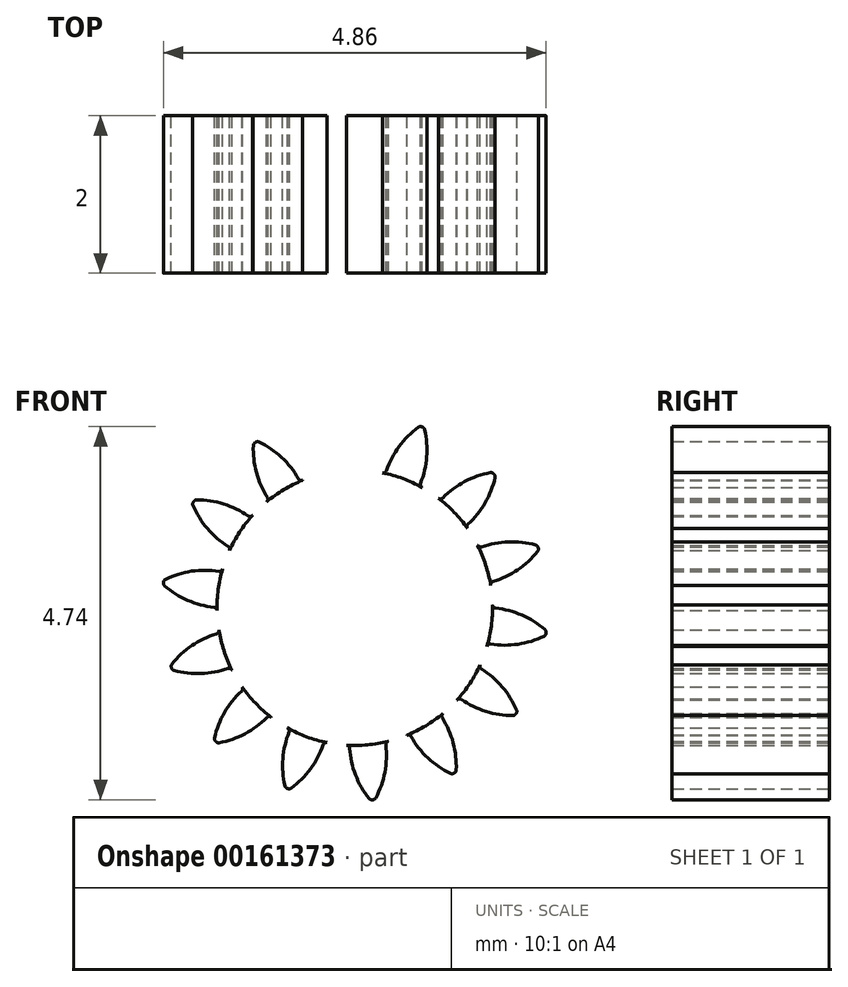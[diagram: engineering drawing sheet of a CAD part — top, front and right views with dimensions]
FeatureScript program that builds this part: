
annotation { "Feature Type Name" : "Feature", "Feature Type Description" : "" }
export const myFeature = defineFeature(function(context is Context, id is Id, definition is map)
    precondition{}
    {
        {
            var Q0;
            Q0=qCreatedBy(makeId("Front.planeOp"),FACE);
            var sketch = newSketch(context, id + "F0", { "sketchPlane" : qUnion([Q0])});
            skCircle(sketch, "E0", {"center": v(0, 0) * mm, "radius": 1.75 * mm, "construction": true});
            skCircle(sketch, "E1", {"center": v(0, 0) * mm, "radius": 2.1 * mm, "construction": true});
            skCircle(sketch, "E2", {"center": v(0, 0) * mm, "radius": 2.45 * mm, "construction": true});
            skLineSegment(sketch, "E3", {"start": v(0, 0) * mm, "end": v(0, 10.28) * mm, "construction": true});
            skLineSegment(sketch, "E4", {"start": v(0, 0) * mm, "end": v(-1.03, 11.12) * mm, "construction": true});
            skLineSegment(sketch, "E5", {"start": v(0, 2.1) * mm, "end": v(-15.76, 2.1) * mm, "construction": true});
            skLineSegment(sketch, "E6", {"start": v(0, 2.1) * mm, "end": v(-14.39, -3.14) * mm, "construction": true});
            skCircle(sketch, "E7", {"center": v(0, 2.1) * mm, "radius": 1.15 * mm, "construction": true});
            skCircle(sketch, "E8", {"center": v(-1.08, 1.7) * mm, "radius": 1.15 * mm, "construction": true});
            skArc(sketch, "E9", {"start": v(-0.18, 2.42) * mm, "mid": v(0, 2.12) * mm, "end": v(0.07, 1.79) * mm});
            skArc(sketch, "E10.MirrorCS", {"start": v(-0.27, 2.42) * mm, "mid": v(-0.38, 2.09) * mm, "end": v(-0.4, 1.74) * mm});
            skArc(sketch, "E11", {"start": v(-0.23, 2.44) * mm, "mid": v(-0.23, 2.44) * mm, "end": v(-0.22, 2.44) * mm});
            skArc(sketch, "E12", {"start": v(-0.43, 1.7) * mm, "mid": v(0.16, -1.74) * mm, "end": v(0.1, 1.75) * mm});
            skPoint(sketch, "E13.visualSharp", {"position": v(-0.39, 1.7) * mm});
            skArc(sketch, "E13.filletArc", {"start": v(-0.43, 1.7) * mm, "mid": v(-0.4, 1.71) * mm, "end": v(-0.4, 1.74) * mm});
            skPoint(sketch, "E14.visualSharp", {"position": v(-0.26, 2.44) * mm});
            skArc(sketch, "E14.filletArc", {"start": v(-0.23, 2.44) * mm, "mid": v(-0.25, 2.43) * mm, "end": v(-0.27, 2.42) * mm});
            skPoint(sketch, "E15.visualSharp", {"position": v(-0.2, 2.44) * mm});
            skArc(sketch, "E15.filletArc", {"start": v(-0.18, 2.42) * mm, "mid": v(-0.2, 2.44) * mm, "end": v(-0.22, 2.44) * mm});
            skPoint(sketch, "E16.visualSharp", {"position": v(0.07, 1.75) * mm});
            skArc(sketch, "E16.filletArc", {"start": v(0.07, 1.79) * mm, "mid": v(0.08, 1.76) * mm, "end": v(0.1, 1.75) * mm});
            skArc(sketch, "E17.1.0", {"start": v(-1.12, 1.34) * mm, "mid": v(-1.1, 1.37) * mm, "end": v(-1.11, 1.4) * mm});
            skArc(sketch, "E17.1.1", {"start": v(-1.29, 2.06) * mm, "mid": v(-1.25, 1.72) * mm, "end": v(-1.11, 1.4) * mm});
            skArc(sketch, "E17.1.2", {"start": v(-1.27, 2.1) * mm, "mid": v(-1.28, 2.08) * mm, "end": v(-1.29, 2.06) * mm});
            skArc(sketch, "E17.1.3", {"start": v(-1.27, 2.1) * mm, "mid": v(-1.26, 2.1) * mm, "end": v(-1.26, 2.1) * mm});
            skArc(sketch, "E17.1.4", {"start": v(-1.22, 2.1) * mm, "mid": v(-1.24, 2.1) * mm, "end": v(-1.26, 2.1) * mm});
            skArc(sketch, "E17.1.5", {"start": v(-1.22, 2.1) * mm, "mid": v(-0.93, 1.9) * mm, "end": v(-0.71, 1.64) * mm});
            skArc(sketch, "E17.1.6", {"start": v(-0.71, 1.64) * mm, "mid": v(-0.7, 1.62) * mm, "end": v(-0.66, 1.62) * mm});
            skArc(sketch, "E17.2.0", {"start": v(-1.6, 0.73) * mm, "mid": v(-1.6, 0.76) * mm, "end": v(-1.6, 0.78) * mm});
            skArc(sketch, "E17.2.1", {"start": v(-2.06, 1.3) * mm, "mid": v(-1.87, 1) * mm, "end": v(-1.6, 0.78) * mm});
            skArc(sketch, "E17.2.2", {"start": v(-2.05, 1.34) * mm, "mid": v(-2.06, 1.32) * mm, "end": v(-2.06, 1.3) * mm});
            skArc(sketch, "E17.2.3", {"start": v(-2.05, 1.34) * mm, "mid": v(-2.05, 1.34) * mm, "end": v(-2.04, 1.35) * mm});
            skArc(sketch, "E17.2.4", {"start": v(-2, 1.37) * mm, "mid": v(-2.03, 1.36) * mm, "end": v(-2.04, 1.35) * mm});
            skArc(sketch, "E17.2.5", {"start": v(-2, 1.37) * mm, "mid": v(-1.67, 1.32) * mm, "end": v(-1.35, 1.17) * mm});
            skArc(sketch, "E17.2.6", {"start": v(-1.35, 1.17) * mm, "mid": v(-1.33, 1.16) * mm, "end": v(-1.3, 1.17) * mm});
            skArc(sketch, "E17.3.0", {"start": v(-1.75, -0.04) * mm, "mid": v(-1.76, 0) * mm, "end": v(-1.79, 0) * mm});
            skArc(sketch, "E17.3.1", {"start": v(-2.42, 0.28) * mm, "mid": v(-2.12, 0.1) * mm, "end": v(-1.79, 0) * mm});
            skArc(sketch, "E17.3.2", {"start": v(-2.43, 0.32) * mm, "mid": v(-2.43, 0.3) * mm, "end": v(-2.42, 0.28) * mm});
            skArc(sketch, "E17.3.3", {"start": v(-2.43, 0.32) * mm, "mid": v(-2.43, 0.32) * mm, "end": v(-2.43, 0.33) * mm});
            skArc(sketch, "E17.3.4", {"start": v(-2.4, 0.36) * mm, "mid": v(-2.42, 0.35) * mm, "end": v(-2.43, 0.33) * mm});
            skArc(sketch, "E17.3.5", {"start": v(-2.4, 0.36) * mm, "mid": v(-2.07, 0.46) * mm, "end": v(-1.73, 0.46) * mm});
            skArc(sketch, "E17.3.6", {"start": v(-1.73, 0.46) * mm, "mid": v(-1.7, 0.47) * mm, "end": v(-1.68, 0.5) * mm});
            skArc(sketch, "E17.4.0", {"start": v(-1.56, -0.8) * mm, "mid": v(-1.58, -0.77) * mm, "end": v(-1.61, -0.77) * mm});
            skArc(sketch, "E17.4.1", {"start": v(-2.3, -0.8) * mm, "mid": v(-1.95, -0.84) * mm, "end": v(-1.61, -0.77) * mm});
            skArc(sketch, "E17.4.2", {"start": v(-2.33, -0.77) * mm, "mid": v(-2.31, -0.79) * mm, "end": v(-2.3, -0.8) * mm});
            skArc(sketch, "E17.4.3", {"start": v(-2.33, -0.77) * mm, "mid": v(-2.33, -0.76) * mm, "end": v(-2.33, -0.76) * mm});
            skArc(sketch, "E17.4.4", {"start": v(-2.32, -0.72) * mm, "mid": v(-2.33, -0.74) * mm, "end": v(-2.33, -0.76) * mm});
            skArc(sketch, "E17.4.5", {"start": v(-2.32, -0.72) * mm, "mid": v(-2.07, -0.48) * mm, "end": v(-1.76, -0.33) * mm});
            skArc(sketch, "E17.4.6", {"start": v(-1.76, -0.33) * mm, "mid": v(-1.73, -0.31) * mm, "end": v(-1.73, -0.29) * mm});
            skArc(sketch, "E17.5.0", {"start": v(-1.06, -1.4) * mm, "mid": v(-1.1, -1.38) * mm, "end": v(-1.12, -1.4) * mm});
            skArc(sketch, "E17.5.1", {"start": v(-1.72, -1.72) * mm, "mid": v(-1.4, -1.6) * mm, "end": v(-1.12, -1.4) * mm});
            skArc(sketch, "E17.5.2", {"start": v(-1.76, -1.7) * mm, "mid": v(-1.74, -1.71) * mm, "end": v(-1.72, -1.72) * mm});
            skArc(sketch, "E17.5.3", {"start": v(-1.76, -1.7) * mm, "mid": v(-1.77, -1.7) * mm, "end": v(-1.77, -1.7) * mm});
            skArc(sketch, "E17.5.4", {"start": v(-1.78, -1.65) * mm, "mid": v(-1.78, -1.67) * mm, "end": v(-1.77, -1.7) * mm});
            skArc(sketch, "E17.5.5", {"start": v(-1.78, -1.65) * mm, "mid": v(-1.66, -1.33) * mm, "end": v(-1.44, -1.06) * mm});
            skArc(sketch, "E17.5.6", {"start": v(-1.44, -1.06) * mm, "mid": v(-1.42, -1.03) * mm, "end": v(-1.43, -1) * mm});
            skArc(sketch, "E17.6.0", {"start": v(-0.35, -1.71) * mm, "mid": v(-0.38, -1.72) * mm, "end": v(-0.4, -1.74) * mm});
            skArc(sketch, "E17.6.1", {"start": v(-0.8, -2.3) * mm, "mid": v(-0.56, -2.05) * mm, "end": v(-0.4, -1.74) * mm});
            skArc(sketch, "E17.6.2", {"start": v(-0.85, -2.3) * mm, "mid": v(-0.83, -2.3) * mm, "end": v(-0.8, -2.3) * mm});
            skArc(sketch, "E17.6.3", {"start": v(-0.85, -2.3) * mm, "mid": v(-0.85, -2.3) * mm, "end": v(-0.86, -2.3) * mm});
            skArc(sketch, "E17.6.4", {"start": v(-0.89, -2.26) * mm, "mid": v(-0.88, -2.28) * mm, "end": v(-0.86, -2.3) * mm});
            skArc(sketch, "E17.6.5", {"start": v(-0.89, -2.26) * mm, "mid": v(-0.91, -1.92) * mm, "end": v(-0.83, -1.58) * mm});
            skArc(sketch, "E17.6.6", {"start": v(-0.83, -1.58) * mm, "mid": v(-0.83, -1.55) * mm, "end": v(-0.85, -1.53) * mm});
            skArc(sketch, "E17.7.0", {"start": v(0.43, -1.7) * mm, "mid": v(0.4, -1.71) * mm, "end": v(0.4, -1.74) * mm});
            skArc(sketch, "E17.7.1", {"start": v(0.27, -2.42) * mm, "mid": v(0.38, -2.09) * mm, "end": v(0.4, -1.74) * mm});
            skArc(sketch, "E17.7.2", {"start": v(0.23, -2.44) * mm, "mid": v(0.25, -2.43) * mm, "end": v(0.27, -2.42) * mm});
            skArc(sketch, "E17.7.3", {"start": v(0.23, -2.44) * mm, "mid": v(0.23, -2.44) * mm, "end": v(0.22, -2.44) * mm});
            skArc(sketch, "E17.7.4", {"start": v(0.18, -2.42) * mm, "mid": v(0.2, -2.44) * mm, "end": v(0.22, -2.44) * mm});
            skArc(sketch, "E17.7.5", {"start": v(0.18, -2.42) * mm, "mid": v(0, -2.12) * mm, "end": v(-0.07, -1.79) * mm});
            skArc(sketch, "E17.7.6", {"start": v(-0.07, -1.79) * mm, "mid": v(-0.08, -1.76) * mm, "end": v(-0.1, -1.75) * mm});
            skArc(sketch, "E17.8.0", {"start": v(1.12, -1.34) * mm, "mid": v(1.1, -1.37) * mm, "end": v(1.11, -1.4) * mm});
            skArc(sketch, "E17.8.1", {"start": v(1.29, -2.06) * mm, "mid": v(1.25, -1.72) * mm, "end": v(1.11, -1.4) * mm});
            skArc(sketch, "E17.8.2", {"start": v(1.27, -2.1) * mm, "mid": v(1.28, -2.08) * mm, "end": v(1.29, -2.06) * mm});
            skArc(sketch, "E17.8.3", {"start": v(1.27, -2.1) * mm, "mid": v(1.26, -2.1) * mm, "end": v(1.26, -2.1) * mm});
            skArc(sketch, "E17.8.4", {"start": v(1.22, -2.1) * mm, "mid": v(1.24, -2.1) * mm, "end": v(1.26, -2.1) * mm});
            skArc(sketch, "E17.8.5", {"start": v(1.22, -2.1) * mm, "mid": v(0.93, -1.9) * mm, "end": v(0.71, -1.64) * mm});
            skArc(sketch, "E17.8.6", {"start": v(0.71, -1.64) * mm, "mid": v(0.7, -1.62) * mm, "end": v(0.66, -1.62) * mm});
            skArc(sketch, "E17.9.0", {"start": v(1.6, -0.73) * mm, "mid": v(1.6, -0.76) * mm, "end": v(1.6, -0.78) * mm});
            skArc(sketch, "E17.9.1", {"start": v(2.06, -1.3) * mm, "mid": v(1.87, -1) * mm, "end": v(1.6, -0.78) * mm});
            skArc(sketch, "E17.9.2", {"start": v(2.05, -1.34) * mm, "mid": v(2.06, -1.32) * mm, "end": v(2.06, -1.3) * mm});
            skArc(sketch, "E17.9.3", {"start": v(2.05, -1.34) * mm, "mid": v(2.05, -1.34) * mm, "end": v(2.04, -1.35) * mm});
            skArc(sketch, "E17.9.4", {"start": v(2, -1.37) * mm, "mid": v(2.03, -1.36) * mm, "end": v(2.04, -1.35) * mm});
            skArc(sketch, "E17.9.5", {"start": v(2, -1.37) * mm, "mid": v(1.67, -1.32) * mm, "end": v(1.35, -1.17) * mm});
            skArc(sketch, "E17.9.6", {"start": v(1.35, -1.17) * mm, "mid": v(1.33, -1.16) * mm, "end": v(1.3, -1.17) * mm});
            skArc(sketch, "E17.10.0", {"start": v(1.75, 0.04) * mm, "mid": v(1.76, 0) * mm, "end": v(1.79, 0) * mm});
            skArc(sketch, "E17.10.1", {"start": v(2.42, -0.28) * mm, "mid": v(2.12, -0.1) * mm, "end": v(1.79, 0) * mm});
            skArc(sketch, "E17.10.2", {"start": v(2.43, -0.32) * mm, "mid": v(2.43, -0.3) * mm, "end": v(2.42, -0.28) * mm});
            skArc(sketch, "E17.10.3", {"start": v(2.43, -0.32) * mm, "mid": v(2.43, -0.32) * mm, "end": v(2.43, -0.33) * mm});
            skArc(sketch, "E17.10.4", {"start": v(2.4, -0.36) * mm, "mid": v(2.42, -0.35) * mm, "end": v(2.43, -0.33) * mm});
            skArc(sketch, "E17.10.5", {"start": v(2.4, -0.36) * mm, "mid": v(2.07, -0.46) * mm, "end": v(1.73, -0.46) * mm});
            skArc(sketch, "E17.10.6", {"start": v(1.73, -0.46) * mm, "mid": v(1.7, -0.47) * mm, "end": v(1.68, -0.5) * mm});
            skArc(sketch, "E17.11.0", {"start": v(1.56, 0.8) * mm, "mid": v(1.58, 0.77) * mm, "end": v(1.61, 0.77) * mm});
            skArc(sketch, "E17.11.1", {"start": v(2.3, 0.8) * mm, "mid": v(1.95, 0.84) * mm, "end": v(1.61, 0.77) * mm});
            skArc(sketch, "E17.11.2", {"start": v(2.33, 0.77) * mm, "mid": v(2.31, 0.79) * mm, "end": v(2.3, 0.8) * mm});
            skArc(sketch, "E17.11.3", {"start": v(2.33, 0.77) * mm, "mid": v(2.33, 0.76) * mm, "end": v(2.33, 0.76) * mm});
            skArc(sketch, "E17.11.4", {"start": v(2.32, 0.72) * mm, "mid": v(2.33, 0.74) * mm, "end": v(2.33, 0.76) * mm});
            skArc(sketch, "E17.11.5", {"start": v(2.32, 0.72) * mm, "mid": v(2.07, 0.48) * mm, "end": v(1.76, 0.33) * mm});
            skArc(sketch, "E17.11.6", {"start": v(1.76, 0.33) * mm, "mid": v(1.73, 0.31) * mm, "end": v(1.73, 0.29) * mm});
            skArc(sketch, "E17.12.0", {"start": v(1.06, 1.4) * mm, "mid": v(1.1, 1.38) * mm, "end": v(1.12, 1.4) * mm});
            skArc(sketch, "E17.12.1", {"start": v(1.72, 1.72) * mm, "mid": v(1.4, 1.6) * mm, "end": v(1.12, 1.4) * mm});
            skArc(sketch, "E17.12.2", {"start": v(1.76, 1.7) * mm, "mid": v(1.74, 1.71) * mm, "end": v(1.72, 1.72) * mm});
            skArc(sketch, "E17.12.3", {"start": v(1.76, 1.7) * mm, "mid": v(1.77, 1.7) * mm, "end": v(1.77, 1.7) * mm});
            skArc(sketch, "E17.12.4", {"start": v(1.78, 1.65) * mm, "mid": v(1.78, 1.67) * mm, "end": v(1.77, 1.7) * mm});
            skArc(sketch, "E17.12.5", {"start": v(1.78, 1.65) * mm, "mid": v(1.66, 1.33) * mm, "end": v(1.44, 1.06) * mm});
            skArc(sketch, "E17.12.6", {"start": v(1.44, 1.06) * mm, "mid": v(1.42, 1.03) * mm, "end": v(1.43, 1) * mm});
            skArc(sketch, "E17.13.0", {"start": v(0.35, 1.71) * mm, "mid": v(0.38, 1.72) * mm, "end": v(0.4, 1.74) * mm});
            skArc(sketch, "E17.13.1", {"start": v(0.8, 2.3) * mm, "mid": v(0.56, 2.05) * mm, "end": v(0.4, 1.74) * mm});
            skArc(sketch, "E17.13.2", {"start": v(0.85, 2.3) * mm, "mid": v(0.83, 2.3) * mm, "end": v(0.8, 2.3) * mm});
            skArc(sketch, "E17.13.3", {"start": v(0.85, 2.3) * mm, "mid": v(0.85, 2.3) * mm, "end": v(0.86, 2.3) * mm});
            skArc(sketch, "E17.13.4", {"start": v(0.89, 2.26) * mm, "mid": v(0.88, 2.28) * mm, "end": v(0.86, 2.3) * mm});
            skArc(sketch, "E17.13.5", {"start": v(0.89, 2.26) * mm, "mid": v(0.91, 1.92) * mm, "end": v(0.83, 1.58) * mm});
            skArc(sketch, "E17.13.6", {"start": v(0.83, 1.58) * mm, "mid": v(0.83, 1.55) * mm, "end": v(0.85, 1.53) * mm});
            skSolve(sketch);
        }
        {
            var Q0;
            Q0=makeQuery(id+"F0.imprint","IMPRINT",FACE,{"disambiguationData":[TD([[makeQuery(id+"F0.imprint","IMPRINT",EDGE,{"derivedFrom":sQuery(id+"F0.wireOp",EDGE,"E9")}),-1.0]])]});
            var Q1;
            {var subQ0=sQuery(id+"F0.wireOp",EDGE,"E17.1.0");Q1=makeQuery(id+"F0.imprint","IMPRINT",FACE,{"disambiguationData":[TD([[makeQuery(id+"F0.imprint","IMPRINT",EDGE,{"derivedFrom":subQ0}),-1.0]])]});}
            var Q2;
            {var subQ0=sQuery(id+"F0.wireOp",EDGE,"E17.2.0");Q2=makeQuery(id+"F0.imprint","IMPRINT",FACE,{"disambiguationData":[TD([[makeQuery(id+"F0.imprint","IMPRINT",EDGE,{"derivedFrom":subQ0}),-1.0]])]});}
            var Q3;
            {var subQ0=sQuery(id+"F0.wireOp",EDGE,"E17.3.0");Q3=makeQuery(id+"F0.imprint","IMPRINT",FACE,{"disambiguationData":[TD([[makeQuery(id+"F0.imprint","IMPRINT",EDGE,{"derivedFrom":subQ0}),-1.0]])]});}
            var Q4;
            {var subQ0=sQuery(id+"F0.wireOp",EDGE,"E17.4.0");Q4=makeQuery(id+"F0.imprint","IMPRINT",FACE,{"disambiguationData":[TD([[makeQuery(id+"F0.imprint","IMPRINT",EDGE,{"derivedFrom":subQ0}),-1.0]])]});}
            var Q5;
            {var subQ0=sQuery(id+"F0.wireOp",EDGE,"E17.16.0");Q5=makeQuery(id+"F0.imprint","IMPRINT",FACE,{"disambiguationData":[TD([[makeQuery(id+"F0.imprint","IMPRINT",EDGE,{"derivedFrom":subQ0}),-1.0]])]});}
            var Q6;
            {var subQ0=sQuery(id+"F0.wireOp",EDGE,"E17.15.0");Q6=makeQuery(id+"F0.imprint","IMPRINT",FACE,{"disambiguationData":[TD([[makeQuery(id+"F0.imprint","IMPRINT",EDGE,{"derivedFrom":subQ0}),-1.0]])]});}
            var Q7;
            {var subQ1=sQuery(id+"F0.wireOp",EDGE,"E17.14.0");Q7=makeQuery(id+"F0.imprint","IMPRINT",FACE,{"disambiguationData":[TD([[makeQuery(id+"F0.imprint","IMPRINT",EDGE,{"derivedFrom":subQ1}),-1.0]])]});}
            var Q8;
            {var subQ0=sQuery(id+"F0.wireOp",EDGE,"E17.13.0");Q8=makeQuery(id+"F0.imprint","IMPRINT",FACE,{"disambiguationData":[TD([[makeQuery(id+"F0.imprint","IMPRINT",EDGE,{"derivedFrom":subQ0}),-1.0]])]});}
            var Q9;
            {var subQ1=sQuery(id+"F0.wireOp",EDGE,"E17.12.0");Q9=makeQuery(id+"F0.imprint","IMPRINT",FACE,{"disambiguationData":[TD([[makeQuery(id+"F0.imprint","IMPRINT",EDGE,{"derivedFrom":subQ1}),-1.0]])]});}
            var Q10;
            {var subQ0=sQuery(id+"F0.wireOp",EDGE,"E17.11.0");Q10=makeQuery(id+"F0.imprint","IMPRINT",FACE,{"disambiguationData":[TD([[makeQuery(id+"F0.imprint","IMPRINT",EDGE,{"derivedFrom":subQ0}),-1.0]])]});}
            var Q11;
            {var subQ0=sQuery(id+"F0.wireOp",EDGE,"E17.10.0");Q11=makeQuery(id+"F0.imprint","IMPRINT",FACE,{"disambiguationData":[TD([[makeQuery(id+"F0.imprint","IMPRINT",EDGE,{"derivedFrom":subQ0}),-1.0]])]});}
            var Q12;
            {var subQ0=sQuery(id+"F0.wireOp",EDGE,"E17.9.0");Q12=makeQuery(id+"F0.imprint","IMPRINT",FACE,{"disambiguationData":[TD([[makeQuery(id+"F0.imprint","IMPRINT",EDGE,{"derivedFrom":subQ0}),-1.0]])]});}
            var Q13;
            {var subQ0=sQuery(id+"F0.wireOp",EDGE,"E17.8.0");Q13=makeQuery(id+"F0.imprint","IMPRINT",FACE,{"disambiguationData":[TD([[makeQuery(id+"F0.imprint","IMPRINT",EDGE,{"derivedFrom":subQ0}),-1.0]])]});}
            var Q14;
            {var subQ0=sQuery(id+"F0.wireOp",EDGE,"E17.7.0");Q14=makeQuery(id+"F0.imprint","IMPRINT",FACE,{"disambiguationData":[TD([[makeQuery(id+"F0.imprint","IMPRINT",EDGE,{"derivedFrom":subQ0}),-1.0]])]});}
            var Q15;
            {var subQ0=sQuery(id+"F0.wireOp",EDGE,"E17.6.0");Q15=makeQuery(id+"F0.imprint","IMPRINT",FACE,{"disambiguationData":[TD([[makeQuery(id+"F0.imprint","IMPRINT",EDGE,{"derivedFrom":subQ0}),-1.0]])]});}
            var Q16;
            {var subQ0=sQuery(id+"F0.wireOp",EDGE,"E17.5.0");Q16=makeQuery(id+"F0.imprint","IMPRINT",FACE,{"disambiguationData":[TD([[makeQuery(id+"F0.imprint","IMPRINT",EDGE,{"derivedFrom":subQ0}),-1.0]])]});}
            extrude(context, id + "F1", {"entities" : qUnion([Q0, Q1, Q2, Q3, Q4, Q5, Q6, Q7, Q8, Q9, Q10, Q11, Q12, Q13, Q14, Q15, Q16]), "depth" : 2 * mm});
        }
        {
            var Q0;
            Q0=makeQuery(id+"F1.opExtrude","CAP_FACE",FACE,{"disambiguationData":[OSD([sQuery(id+"F0.wireOp",EDGE,"E9"),sQuery(id+"F0.wireOp",EDGE,"E10.MirrorCS"),sQuery(id+"F0.wireOp",EDGE,"E11"),sQuery(id+"F0.wireOp",EDGE,"E12"),sQuery(id+"F0.wireOp",EDGE,"E13.filletArc"),sQuery(id+"F0.wireOp",EDGE,"E14.filletArc"),sQuery(id+"F0.wireOp",EDGE,"E15.filletArc"),sQuery(id+"F0.wireOp",EDGE,"E16.filletArc"),sQuery(id+"F0.wireOp",EDGE,"E17.1.0"),sQuery(id+"F0.wireOp",EDGE,"E17.1.1"),sQuery(id+"F0.wireOp",EDGE,"E17.1.2"),sQuery(id+"F0.wireOp",EDGE,"E17.1.3"),sQuery(id+"F0.wireOp",EDGE,"E17.1.4"),sQuery(id+"F0.wireOp",EDGE,"E17.1.5"),sQuery(id+"F0.wireOp",EDGE,"E17.1.6"),sQuery(id+"F0.wireOp",EDGE,"E17.2.0"),sQuery(id+"F0.wireOp",EDGE,"E17.2.1"),sQuery(id+"F0.wireOp",EDGE,"E17.2.2"),sQuery(id+"F0.wireOp",EDGE,"E17.2.3"),sQuery(id+"F0.wireOp",EDGE,"E17.2.4"),sQuery(id+"F0.wireOp",EDGE,"E17.2.5"),sQuery(id+"F0.wireOp",EDGE,"E17.2.6"),sQuery(id+"F0.wireOp",EDGE,"E17.3.0"),sQuery(id+"F0.wireOp",EDGE,"E17.3.1"),sQuery(id+"F0.wireOp",EDGE,"E17.3.2"),sQuery(id+"F0.wireOp",EDGE,"E17.3.3"),sQuery(id+"F0.wireOp",EDGE,"E17.3.4"),sQuery(id+"F0.wireOp",EDGE,"E17.3.5"),sQuery(id+"F0.wireOp",EDGE,"E17.3.6"),sQuery(id+"F0.wireOp",EDGE,"E17.4.0"),sQuery(id+"F0.wireOp",EDGE,"E17.4.1"),sQuery(id+"F0.wireOp",EDGE,"E17.4.2"),sQuery(id+"F0.wireOp",EDGE,"E17.4.3"),sQuery(id+"F0.wireOp",EDGE,"E17.4.4"),sQuery(id+"F0.wireOp",EDGE,"E17.4.5"),sQuery(id+"F0.wireOp",EDGE,"E17.4.6"),sQuery(id+"F0.wireOp",EDGE,"E17.5.0"),sQuery(id+"F0.wireOp",EDGE,"E17.5.1"),sQuery(id+"F0.wireOp",EDGE,"E17.5.2"),sQuery(id+"F0.wireOp",EDGE,"E17.5.3"),sQuery(id+"F0.wireOp",EDGE,"E17.5.4"),sQuery(id+"F0.wireOp",EDGE,"E17.5.5"),sQuery(id+"F0.wireOp",EDGE,"E17.5.6"),sQuery(id+"F0.wireOp",EDGE,"E17.6.0"),sQuery(id+"F0.wireOp",EDGE,"E17.6.1"),sQuery(id+"F0.wireOp",EDGE,"E17.6.2"),sQuery(id+"F0.wireOp",EDGE,"E17.6.3"),sQuery(id+"F0.wireOp",EDGE,"E17.6.4"),sQuery(id+"F0.wireOp",EDGE,"E17.6.5"),sQuery(id+"F0.wireOp",EDGE,"E17.6.6"),sQuery(id+"F0.wireOp",EDGE,"E17.7.0"),sQuery(id+"F0.wireOp",EDGE,"E17.7.1"),sQuery(id+"F0.wireOp",EDGE,"E17.7.2"),sQuery(id+"F0.wireOp",EDGE,"E17.7.3"),sQuery(id+"F0.wireOp",EDGE,"E17.7.4"),sQuery(id+"F0.wireOp",EDGE,"E17.7.5"),sQuery(id+"F0.wireOp",EDGE,"E17.7.6"),sQuery(id+"F0.wireOp",EDGE,"E17.8.0"),sQuery(id+"F0.wireOp",EDGE,"E17.8.1"),sQuery(id+"F0.wireOp",EDGE,"E17.8.2"),sQuery(id+"F0.wireOp",EDGE,"E17.8.3"),sQuery(id+"F0.wireOp",EDGE,"E17.8.4"),sQuery(id+"F0.wireOp",EDGE,"E17.8.5"),sQuery(id+"F0.wireOp",EDGE,"E17.8.6"),sQuery(id+"F0.wireOp",EDGE,"E17.9.0"),sQuery(id+"F0.wireOp",EDGE,"E17.9.1"),sQuery(id+"F0.wireOp",EDGE,"E17.9.2"),sQuery(id+"F0.wireOp",EDGE,"E17.9.3"),sQuery(id+"F0.wireOp",EDGE,"E17.9.4"),sQuery(id+"F0.wireOp",EDGE,"E17.9.5"),sQuery(id+"F0.wireOp",EDGE,"E17.9.6"),sQuery(id+"F0.wireOp",EDGE,"E17.10.0"),sQuery(id+"F0.wireOp",EDGE,"E17.10.1"),sQuery(id+"F0.wireOp",EDGE,"E17.10.2"),sQuery(id+"F0.wireOp",EDGE,"E17.10.3"),sQuery(id+"F0.wireOp",EDGE,"E17.10.4"),sQuery(id+"F0.wireOp",EDGE,"E17.10.5"),sQuery(id+"F0.wireOp",EDGE,"E17.10.6"),sQuery(id+"F0.wireOp",EDGE,"E17.11.0"),sQuery(id+"F0.wireOp",EDGE,"E17.11.1"),sQuery(id+"F0.wireOp",EDGE,"E17.11.2"),sQuery(id+"F0.wireOp",EDGE,"E17.11.3"),sQuery(id+"F0.wireOp",EDGE,"E17.11.4"),sQuery(id+"F0.wireOp",EDGE,"E17.11.5"),sQuery(id+"F0.wireOp",EDGE,"E17.11.6"),sQuery(id+"F0.wireOp",EDGE,"E17.12.0"),sQuery(id+"F0.wireOp",EDGE,"E17.12.1"),sQuery(id+"F0.wireOp",EDGE,"E17.12.2"),sQuery(id+"F0.wireOp",EDGE,"E17.12.3"),sQuery(id+"F0.wireOp",EDGE,"E17.12.4"),sQuery(id+"F0.wireOp",EDGE,"E17.12.5"),sQuery(id+"F0.wireOp",EDGE,"E17.12.6"),sQuery(id+"F0.wireOp",EDGE,"E17.13.0"),sQuery(id+"F0.wireOp",EDGE,"E17.13.1"),sQuery(id+"F0.wireOp",EDGE,"E17.13.2"),sQuery(id+"F0.wireOp",EDGE,"E17.13.3"),sQuery(id+"F0.wireOp",EDGE,"E17.13.4"),sQuery(id+"F0.wireOp",EDGE,"E17.13.5"),sQuery(id+"F0.wireOp",EDGE,"E17.13.6"),sQuery(id+"F0.wireOp",EDGE,"E17.14.0"),sQuery(id+"F0.wireOp",EDGE,"E17.14.1"),sQuery(id+"F0.wireOp",EDGE,"E17.14.2"),sQuery(id+"F0.wireOp",EDGE,"E17.14.3"),sQuery(id+"F0.wireOp",EDGE,"E17.14.4"),sQuery(id+"F0.wireOp",EDGE,"E17.14.5"),sQuery(id+"F0.wireOp",EDGE,"E17.14.6"),sQuery(id+"F0.wireOp",EDGE,"E17.15.0"),sQuery(id+"F0.wireOp",EDGE,"E17.15.1"),sQuery(id+"F0.wireOp",EDGE,"E17.15.2"),sQuery(id+"F0.wireOp",EDGE,"E17.15.3"),sQuery(id+"F0.wireOp",EDGE,"E17.15.4"),sQuery(id+"F0.wireOp",EDGE,"E17.15.5"),sQuery(id+"F0.wireOp",EDGE,"E17.15.6"),sQuery(id+"F0.wireOp",EDGE,"E17.16.0"),sQuery(id+"F0.wireOp",EDGE,"E17.16.1"),sQuery(id+"F0.wireOp",EDGE,"E17.16.2"),sQuery(id+"F0.wireOp",EDGE,"E17.16.3"),sQuery(id+"F0.wireOp",EDGE,"E17.16.4"),sQuery(id+"F0.wireOp",EDGE,"E17.16.5"),sQuery(id+"F0.wireOp",EDGE,"E17.16.6")])],"isStart":false});
            var sketch = newSketch(context, id + "F2", { "sketchPlane" : qUnion([Q0])});
            skCircle(sketch, "E18", {"center": v(0, 0) * mm, "radius": 1.1 * mm});
            skSolve(sketch);
        }
        {
            var Q0;
            Q0=qSketchRegion(id+"F2",true);
            extrude(context, id + "F3", {"entities" : qUnion([Q0]), "operationType" : NewBodyOperationType.REMOVE, "endBound" : BoundingType.THROUGH_ALL, "oppositeDirection" : true, "depth" : 25 * mm});
        }
    });
